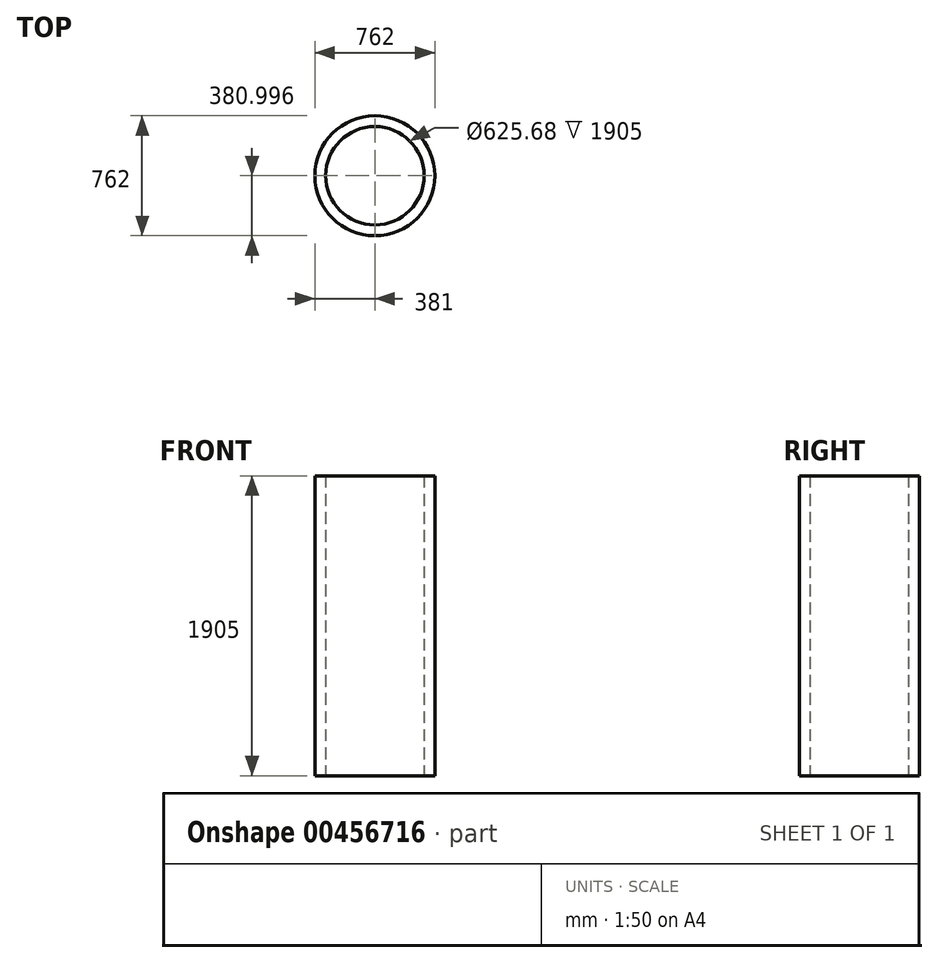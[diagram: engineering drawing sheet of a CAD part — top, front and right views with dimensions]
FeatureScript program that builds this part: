
annotation { "Feature Type Name" : "Feature", "Feature Type Description" : "" }
export const myFeature = defineFeature(function(context is Context, id is Id, definition is map)
    precondition{}
    {
        {
            var Q0;
            Q0=qCreatedBy(makeId("Top.planeOp"),FACE);
            var sketch = newSketch(context, id + "F0", { "sketchPlane" : qUnion([Q0])});
            skCircle(sketch, "E0", {"center": v(0, 68.14) * mm, "radius": 381 * mm});
            skCircle(sketch, "E1", {"center": v(0, 68.14) * mm, "radius": 312.84 * mm});
            skSolve(sketch);
        }
        {
            var Q0;
            Q0=makeQuery(id+"F0.imprint","IMPRINT",FACE,{"disambiguationData":[TD([[makeQuery(id+"F0.imprint","IMPRINT",EDGE,{"derivedFrom":sQuery(id+"F0.wireOp",EDGE,"E0")}),1.0]])]});
            var Q1;
            Q1 = qSketchRegion(id + "F0", true);
            extrude(context, id + "F1", {"entities" : qUnion([Q0, Q1]), "depth" : 25.4 * mm});
        }
        {
            var Q0;
            Q0 = qSketchRegion(id + "F0", true);
            extrude(context, id + "F2", {"entities" : qUnion([Q0]), "operationType" : NewBodyOperationType.ADD, "depth" : 1905 * mm});
        }
    });
